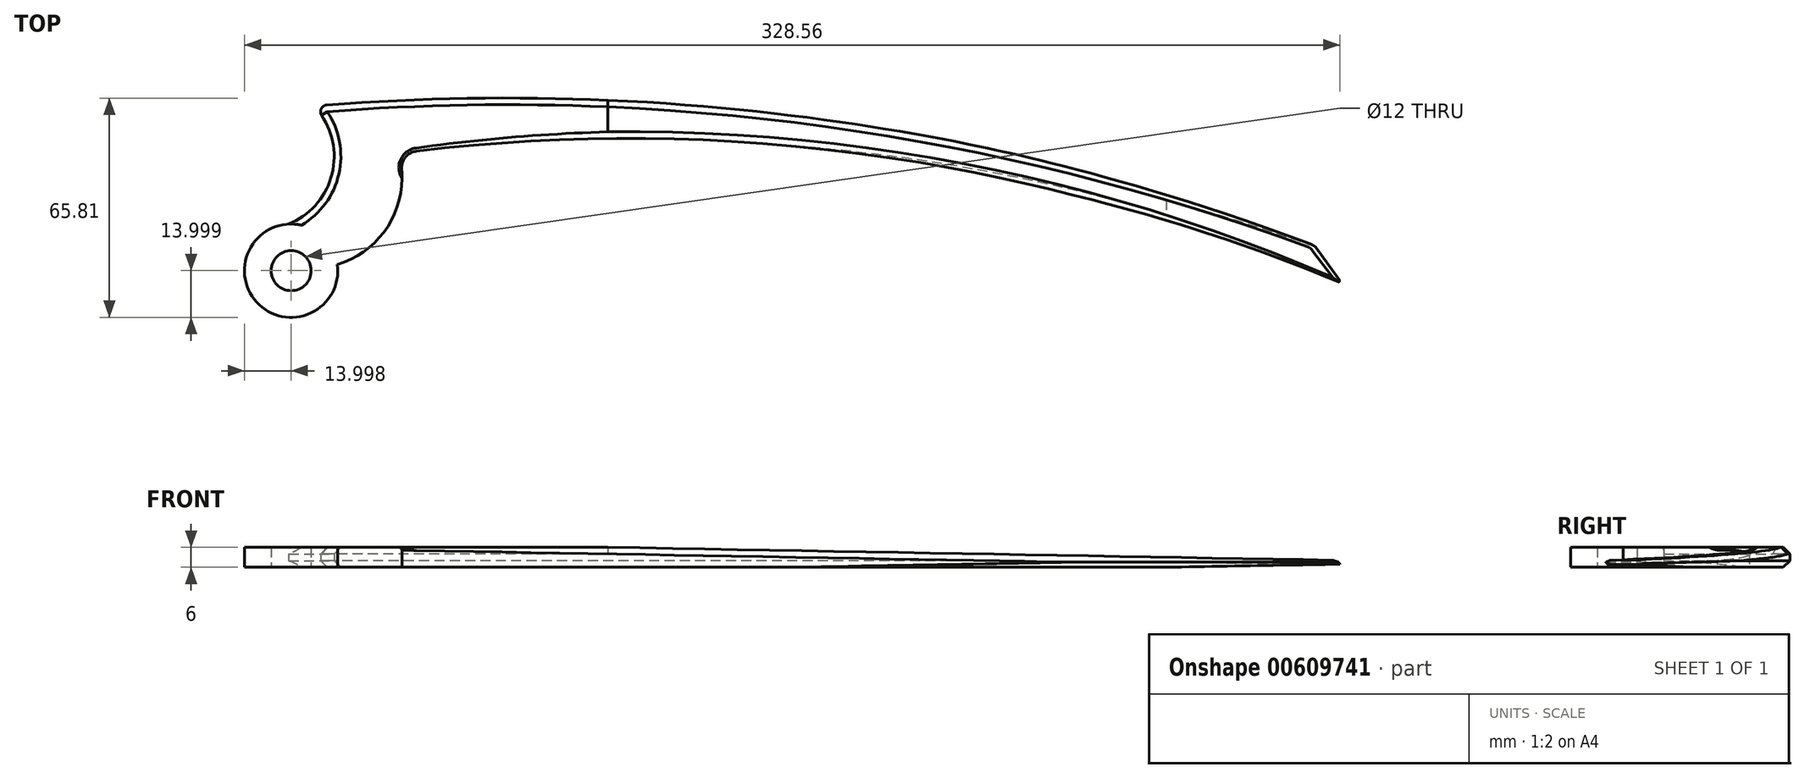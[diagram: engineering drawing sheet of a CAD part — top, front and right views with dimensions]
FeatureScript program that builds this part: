
annotation { "Feature Type Name" : "Feature", "Feature Type Description" : "" }
export const myFeature = defineFeature(function(context is Context, id is Id, definition is map)
    precondition{}
    {
        {
            var Q0;
            Q0=qCreatedBy(makeId("Top.planeOp"),FACE);
            var sketch = newSketch(context, id + "F0", { "sketchPlane" : qUnion([Q0])});
            skCircle(sketch, "E0", {"center": v(-118.82, 19.04) * mm, "radius": 14 * mm});
            skArc(sketch, "E1", {"start": v(-119.55, 33.02) * mm, "mid": v(-106.86, 47) * mm, "end": v(-109.66, 65.66) * mm});
            skArc(sketch, "E2", {"start": v(186.71, 28.1) * mm, "mid": v(41.46, 64.29) * mm, "end": v(-108.16, 68.77) * mm});
            skArc(sketch, "E3", {"start": v(-104.94, 20.87) * mm, "mid": v(-90.2, 31.74) * mm, "end": v(-85.66, 49.48) * mm});
            skLineSegment(sketch, "E4", {"start": v(188.98, 26.43) * mm, "end": v(199.85, 12.08) * mm});
            skArc(sketch, "E5", {"start": v(199.85, 12.08) * mm, "mid": v(62.2, 52.7) * mm, "end": v(-81.29, 54.9) * mm});
            skPoint(sketch, "E6.visualSharp", {"position": v(-86.53, 54.24) * mm});
            skArc(sketch, "E6.filletArc", {"start": v(-81.29, 54.9) * mm, "mid": v(-84.57, 53.08) * mm, "end": v(-85.66, 49.48) * mm});
            skPoint(sketch, "E7.visualSharp", {"position": v(-111.9, 68.47) * mm});
            skArc(sketch, "E7.filletArc", {"start": v(-108.16, 68.77) * mm, "mid": v(-109.8, 67.65) * mm, "end": v(-109.66, 65.66) * mm});
            skPoint(sketch, "E8.visualSharp", {"position": v(188.1, 27.6) * mm});
            skArc(sketch, "E8.filletArc", {"start": v(188.98, 26.43) * mm, "mid": v(187.96, 27.43) * mm, "end": v(186.71, 28.1) * mm});
            skCircle(sketch, "E9", {"center": v(-118.82, 19.04) * mm, "radius": 6 * mm});
            skSolve(sketch);
        }
        {
            var Q0;
            Q0 = qSketchRegion(id + "F0", true);
            extrude(context, id + "F1", {"entities" : qUnion([Q0]), "depth" : 6 * mm, "offsetDistance" : 25 * mm});
        }
        {
            var Q0;
            Q0=qCreatedBy(makeId("Front.planeOp"),FACE);
            var sketch = newSketch(context, id + "F2", { "sketchPlane" : qUnion([Q0])});
            skLineSegment(sketch, "E10", {"start": v(227.38, 1.5) * mm, "end": v(-107.62, -4.5) * mm});
            skLineSegment(sketch, "E11", {"start": v(-107.62, -4.5) * mm, "end": v(262.38, -4.5) * mm});
            skLineSegment(sketch, "E12", {"start": v(262.38, -4.5) * mm, "end": v(262.38, 7.5) * mm});
            skLineSegment(sketch, "E13", {"start": v(227.38, 1.5) * mm, "end": v(-107.62, 7.5) * mm});
            skLineSegment(sketch, "E14", {"start": v(-107.62, 7.5) * mm, "end": v(262.38, 7.5) * mm});
            skSolve(sketch);
        }
        {
            var Q0;
            Q0 = qSketchRegion(id + "F2", true);
            extrude(context, id + "F3", {"entities" : qUnion([Q0]), "operationType" : NewBodyOperationType.REMOVE, "oppositeDirection" : true, "depth" : 111 * mm, "offsetDistance" : 25 * mm});
        }
        {
            var Q0;
            Q0=makeQuery(id+"F1.opExtrude","CAP_EDGE",EDGE,{"disambiguationData":[OSD([sQuery(id+"F0.wireOp",EDGE,"E2")])],"isStart":true});
            var Q1;
            Q1=makeQuery(id+"F1.opExtrude","CAP_EDGE",EDGE,{"disambiguationData":[OSD([sQuery(id+"F0.wireOp",EDGE,"E2")])],"isStart":false});
            chamfer(context, id + "F4", {"entities" : qUnion([Q0, Q1]), "width" : 2 * mm, "tangentPropagation" : true});
        }
        {
            var Q0;
            Q0=makeQuery(id+"F3.boolean.opBoolean","INTERSECT",EDGE,{"derivedFrom":[makeQuery(id+"F1.opExtrude","SWEPT_FACE",FACE,{"disambiguationData":[OSD([sQuery(id+"F0.wireOp",EDGE,"E5")])]}),makeQuery(id+"F3.opExtrude","SWEPT_FACE",FACE,{"disambiguationData":[OSD([sQuery(id+"F2.wireOp",EDGE,"E10")])]})]});
            var Q1;
            Q1=makeQuery(id+"F3.boolean.opBoolean","INTERSECT",EDGE,{"derivedFrom":[makeQuery(id+"F1.opExtrude","SWEPT_FACE",FACE,{"disambiguationData":[OSD([sQuery(id+"F0.wireOp",EDGE,"E5")])]}),makeQuery(id+"F3.opExtrude","SWEPT_FACE",FACE,{"disambiguationData":[OSD([sQuery(id+"F2.wireOp",EDGE,"E13")])]})]});
            chamfer(context, id + "F5", {"entities" : qUnion([Q0, Q1]), "width" : 2 * mm, "tangentPropagation" : true});
        }
        {
            var Q0;
            Q0=makeQuery(id+"F3.boolean.opBoolean","INTERSECT",EDGE,{"derivedFrom":[makeQuery(id+"F1.opExtrude","SWEPT_FACE",FACE,{"disambiguationData":[OSD([sQuery(id+"F0.wireOp",EDGE,"E4")])]}),makeQuery(id+"F3.opExtrude","SWEPT_FACE",FACE,{"disambiguationData":[OSD([sQuery(id+"F2.wireOp",EDGE,"E13")])]})]});
            var Q1;
            Q1=makeQuery(id+"F3.boolean.opBoolean","INTERSECT",EDGE,{"derivedFrom":[makeQuery(id+"F1.opExtrude","SWEPT_FACE",FACE,{"disambiguationData":[OSD([sQuery(id+"F0.wireOp",EDGE,"E2")])]}),makeQuery(id+"F3.opExtrude","SWEPT_FACE",FACE,{"disambiguationData":[OSD([sQuery(id+"F2.wireOp",EDGE,"E13")])]})]});
            chamfer(context, id + "F6", {"entities" : qUnion([Q0, Q1]), "width" : 2 * mm, "tangentPropagation" : true});
        }
    });
